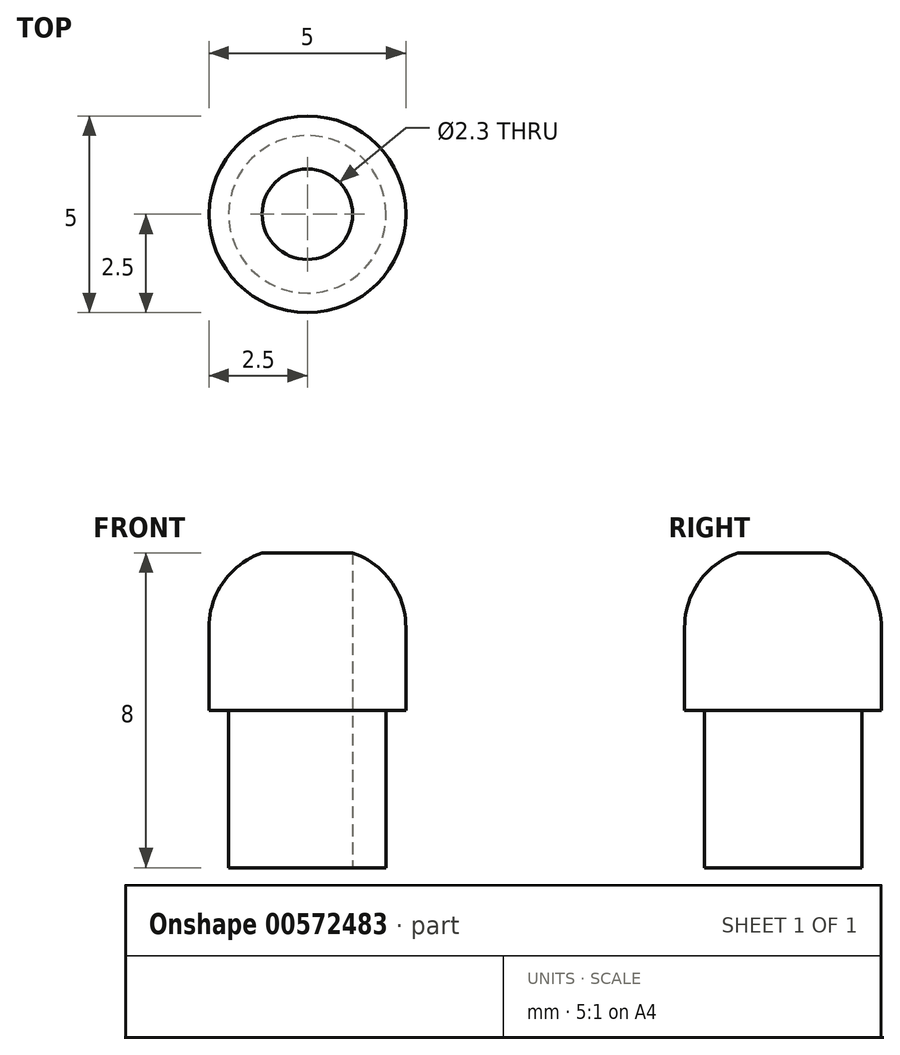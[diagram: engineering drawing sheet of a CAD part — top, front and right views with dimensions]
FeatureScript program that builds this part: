
annotation { "Feature Type Name" : "Feature", "Feature Type Description" : "" }
export const myFeature = defineFeature(function(context is Context, id is Id, definition is map)
    precondition{}
    {
        {
            var Q0;
            Q0=qCreatedBy(makeId("Top.planeOp"),FACE);
            var sketch = newSketch(context, id + "F0", { "sketchPlane" : qUnion([Q0])});
            skCircle(sketch, "E0", {"center": v(0, 0) * mm, "radius": 1.15 * mm});
            skCircle(sketch, "E1", {"center": v(0, 0) * mm, "radius": 2 * mm});
            skSolve(sketch);
        }
        {
            var Q0;
            Q0 = qSketchRegion(id + "F0", true);
            extrude(context, id + "F1", {"entities" : qUnion([Q0]), "depth" : 8 * mm, "offsetDistance" : 25 * mm});
        }
        {
            var Q0;
            Q0=makeQuery(id+"F1.opExtrude","CAP_FACE",FACE,{"disambiguationData":[OSD([sQuery(id+"F0.wireOp",EDGE,"E0"),sQuery(id+"F0.wireOp",EDGE,"E1")])],"isStart":false});
            cPlane(context, id + "F2", {"entities" : qUnion([Q0]), "cplaneType" : CPlaneType.OFFSET, "offset" : 4 * mm, "oppositeDirection" : true, "width" : 150 * mm, "height" : 150 * mm});
        }
        {
            var Q0;
            Q0=qCreatedBy(id+"F2.planeOp",FACE);
            var sketch = newSketch(context, id + "F3", { "sketchPlane" : qUnion([Q0])});
            skCircle(sketch, "E2.0", {"center": v(0, 0) * mm, "radius": 2 * mm});
            skCircle(sketch, "E3", {"center": v(0, 0) * mm, "radius": 2.5 * mm});
            skSolve(sketch);
        }
        {
            var Q0;
            Q0=makeQuery(id+"F3.imprint","IMPRINT",FACE,{"disambiguationData":[TD([[makeQuery(id+"F3.imprint","IMPRINT",EDGE,{"derivedFrom":sQuery(id+"F3.wireOp",EDGE,"E2.0")}),-1.0]])]});
            var Q1;
            Q1=makeQuery(id+"F1.opExtrude","CAP_FACE",FACE,{"disambiguationData":[OSD([sQuery(id+"F0.wireOp",EDGE,"E0"),sQuery(id+"F0.wireOp",EDGE,"E1")])],"isStart":false});
            extrude(context, id + "F4", {"entities" : qUnion([Q0]), "operationType" : NewBodyOperationType.ADD, "endBound" : BoundingType.UP_TO_SURFACE, "depth" : 25 * mm, "endBoundEntityFace" : qUnion([Q1]), "offsetDistance" : 25 * mm});
        }
        {
            var Q0;
            Q0=makeQuery(id+"F4.opExtrude","CAP_EDGE",EDGE,{"disambiguationData":[OSD([sQuery(id+"F3.wireOp",EDGE,"E3")])],"isStart":false});
            fillet(context, id + "F5", {"entities" : qUnion([Q0]), "radius" : 2 * mm, "tangentPropagation" : true, "allowEdgeOverflow" : false});
        }
    });
